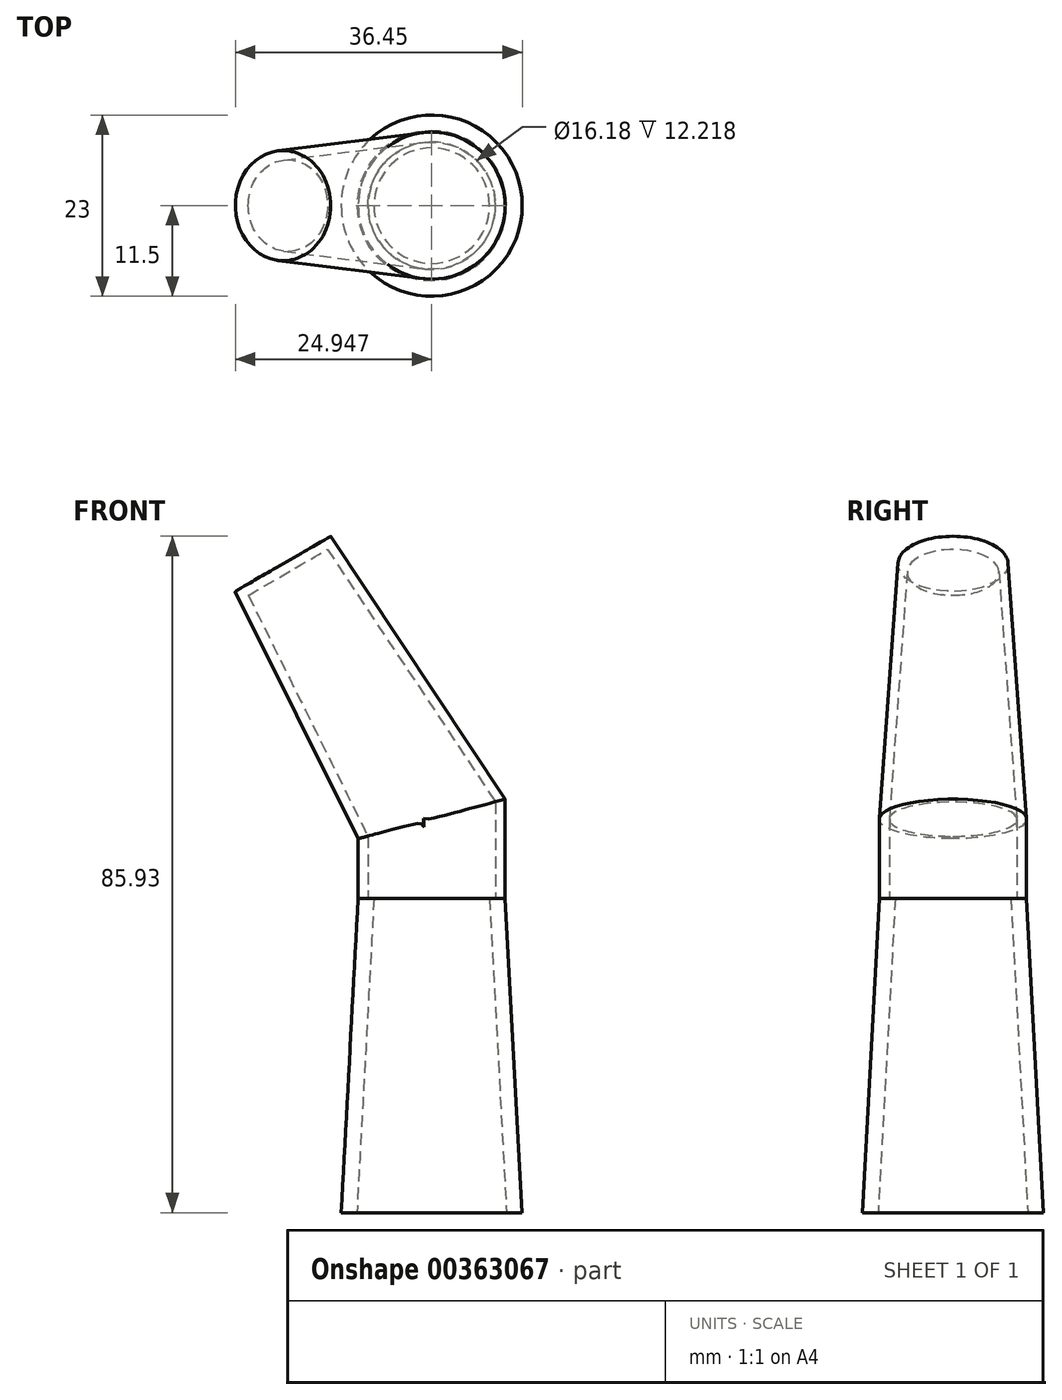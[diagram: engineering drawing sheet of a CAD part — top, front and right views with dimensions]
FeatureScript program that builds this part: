
annotation { "Feature Type Name" : "Feature", "Feature Type Description" : "" }
export const myFeature = defineFeature(function(context is Context, id is Id, definition is map)
    precondition{}
    {
        {
            var Q0;
            Q0=qCreatedBy(makeId("Front.planeOp"),FACE);
            var sketch = newSketch(context, id + "F0", { "sketchPlane" : qUnion([Q0])});
            skLineSegment(sketch, "E0", {"start": v(0, 7.84) * mm, "end": v(8.23, 12.6) * mm});
            skLineSegment(sketch, "E1", {"start": v(8.23, 12.6) * mm, "end": v(-13.94, 45.99) * mm});
            skLineSegment(sketch, "E2", {"start": v(-13.94, 45.99) * mm, "end": v(-20, 42.49) * mm});
            skLineSegment(sketch, "E3", {"start": v(-20, 42.49) * mm, "end": v(0, 7.84) * mm});
            skLineSegment(sketch, "E4", {"start": v(0, 7.84) * mm, "end": v(0, 0) * mm, "construction": true});
            skSolve(sketch);
        }
        {
            var Q0;
            Q0 = qSketchRegion(id + "F0", true);
            var Q1;
            Q1=sQuery(id+"F0.wireOp",EDGE,"E3");
            revolve(context, id + "F1", {"entities" : qUnion([Q0]), "axis" : qUnion([Q1]), "revolveType" : RevolveType.FULL});
        }
        {
            var Q0;
            Q0=qCreatedBy(makeId("Top.planeOp"),FACE);
            var sketch = newSketch(context, id + "F2", { "sketchPlane" : qUnion([Q0])});
            skCircle(sketch, "E5", {"center": v(-1.11, 0) * mm, "radius": 9.34 * mm});
            skEllipticalArc(sketch, "E6.0", {"construction": true});
            skEllipticalArc(sketch, "E7.0", {"construction": true});
            skLineSegment(sketch, "E8", {"start": v(-20, -7) * mm, "end": v(-0.9, -9.44) * mm, "construction": true});
            skLineSegment(sketch, "E9", {"start": v(-20, 7) * mm, "end": v(-0.9, 9.44) * mm, "construction": true});
            skPoint(sketch, "E10.orphan", {"position": v(0, -9.56) * mm});
            const initialGuessF2  = {"E6.0": [0, 0, 0, 1, 0.0095, 0.008227241335952169, 3.031273238553991, 0.11031941503580245], "E7.0": [-0.02, 0, 0, 1, 0.007, 0.006062177826491076, 0, 3.141592653589793]};
            skSetInitialGuess(sketch, initialGuessF2);
            skSolve(sketch);
        }
        {
            var Q0;
            Q0 = qSketchRegion(id + "F2", true);
            var Q1;
            Q1=makeQuery(id+"F1.opRevolve","SWEPT_BODY",BODY,{"disambiguationData":[OSD([sQuery(id+"F0.wireOp",EDGE,"E0"),sQuery(id+"F0.wireOp",EDGE,"E1"),sQuery(id+"F0.wireOp",EDGE,"E2"),sQuery(id+"F0.wireOp",EDGE,"E3")])]});
            extrude(context, id + "F3", {"entities" : qUnion([Q0]), "operationType" : NewBodyOperationType.ADD, "endBound" : BoundingType.UP_TO_BODY, "endBoundEntityBody" : qUnion([Q1]), "depth" : 25 * mm});
        }
        {
            var Q0;
            Q0=makeQuery(id+"F3.opExtrude","CAP_FACE",FACE,{"disambiguationData":[OSD([sQuery(id+"F2.wireOp",EDGE,"E5")])],"isStart":true});
            var sketch = newSketch(context, id + "F4", { "sketchPlane" : qUnion([Q0])});
            skArc(sketch, "E11.0", {"start": v(-2.17, -9.28) * mm, "mid": v(8.23, 0) * mm, "end": v(-2.17, 9.28) * mm});
            skArc(sketch, "E12.0", {"start": v(-2.29, -10.27) * mm, "mid": v(9.23, 0) * mm, "end": v(-2.29, 10.27) * mm});
            skLineSegment(sketch, "E13", {"start": v(-2.17, 9.28) * mm, "end": v(-2.29, 10.27) * mm});
            skLineSegment(sketch, "E14.MirrorCS", {"start": v(-2.17, -9.28) * mm, "end": v(-2.29, -10.27) * mm});
            skSolve(sketch);
        }
        {
            var Q0;
            Q0 = qSketchRegion(id + "F4", true);
            extrude(context, id + "F5", {"entities" : qUnion([Q0]), "operationType" : NewBodyOperationType.REMOVE, "oppositeDirection" : true, "depth" : 25 * mm});
        }
        {
            var Q0;
            Q0=qCreatedBy(makeId("Front.planeOp"),FACE);
            var sketch = newSketch(context, id + "F6", { "sketchPlane" : qUnion([Q0])});
            skLineSegment(sketch, "E15.0.0", {"start": v(-8.45, 0) * mm, "end": v(-10.45, 0) * mm});
            skLineSegment(sketch, "E16", {"start": v(-10.45, 0) * mm, "end": v(-12.61, -39.94) * mm});
            skLineSegment(sketch, "E17", {"start": v(-12.61, -39.94) * mm, "end": v(-10.61, -39.94) * mm});
            skLineSegment(sketch, "E18", {"start": v(-10.61, -39.94) * mm, "end": v(-8.45, 0) * mm});
            skPoint(sketch, "E19.orphan", {"position": v(8.23, 0) * mm});
            skLineSegment(sketch, "E20", {"start": v(-1.11, -39.94) * mm, "end": v(-1.11, 0) * mm, "construction": true});
            skLineSegment(sketch, "E21.0.0", {"start": v(8.23, 0) * mm, "end": v(-10.45, 0) * mm, "construction": true});
            skSolve(sketch);
        }
        {
            var Q0;
            Q0 = qSketchRegion(id + "F6", true);
            var Q1;
            Q1=sQuery(id+"F6.wireOp",EDGE,"E20");
            revolve(context, id + "F7", {"operationType" : NewBodyOperationType.ADD, "entities" : qUnion([Q0]), "axis" : qUnion([Q1]), "revolveType" : RevolveType.FULL});
        }
        {
            var Q0;
            Q0=makeQuery(id+"F3.opExtrude","CAP_FACE",FACE,{"disambiguationData":[OSD([sQuery(id+"F2.wireOp",EDGE,"E5")])],"isStart":true});
            shell(context, id + "F8", {"entities" : qUnion([Q0]), "thickness" : 1.25 * mm});
        }
    });
